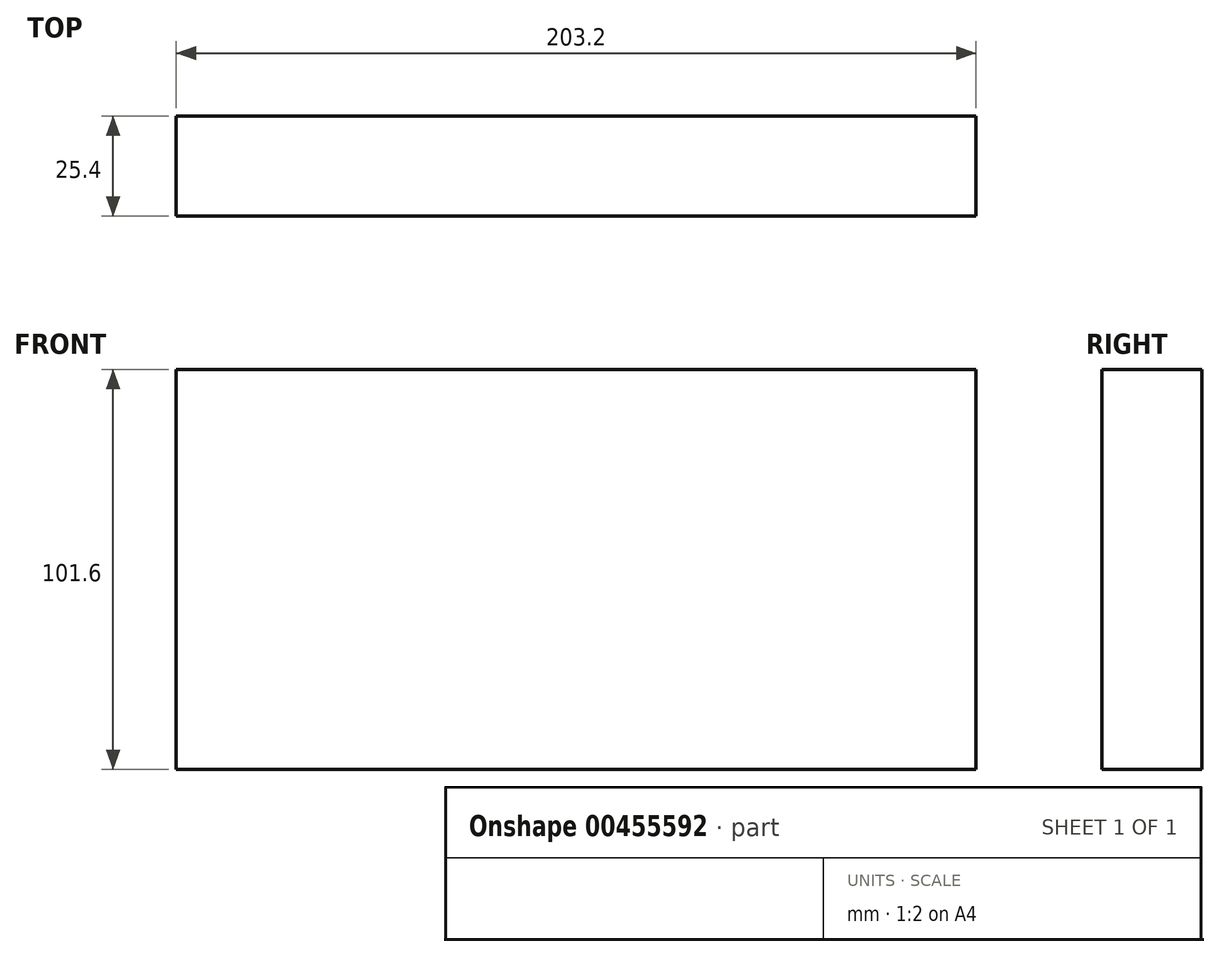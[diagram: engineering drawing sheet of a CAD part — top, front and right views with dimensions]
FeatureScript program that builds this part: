
annotation { "Feature Type Name" : "Feature", "Feature Type Description" : "" }
export const myFeature = defineFeature(function(context is Context, id is Id, definition is map)
    precondition{}
    {
        {
            var Q0;
            Q0=qCreatedBy(makeId("Front.planeOp"),FACE);
            var sketch = newSketch(context, id + "F0", { "sketchPlane" : qUnion([Q0])});
            skLineSegment(sketch, "E0.bottom", {"start": v(101.6, 50.8) * mm, "end": v(-101.6, 50.8) * mm});
            skLineSegment(sketch, "E0.top", {"start": v(101.6, -50.8) * mm, "end": v(-101.6, -50.8) * mm});
            skLineSegment(sketch, "E0.left", {"start": v(101.6, 50.8) * mm, "end": v(101.6, -50.8) * mm});
            skLineSegment(sketch, "E0.right", {"start": v(-101.6, 50.8) * mm, "end": v(-101.6, -50.8) * mm});
            skPoint(sketch, "E0.middle", {"position": v(0, 0) * mm});
            skSolve(sketch);
        }
        {
            var Q0;
            Q0 = qSketchRegion(id + "F0", true);
            extrude(context, id + "F1", {"entities" : qUnion([Q0]), "depth" : 25.4 * mm});
        }
    });
